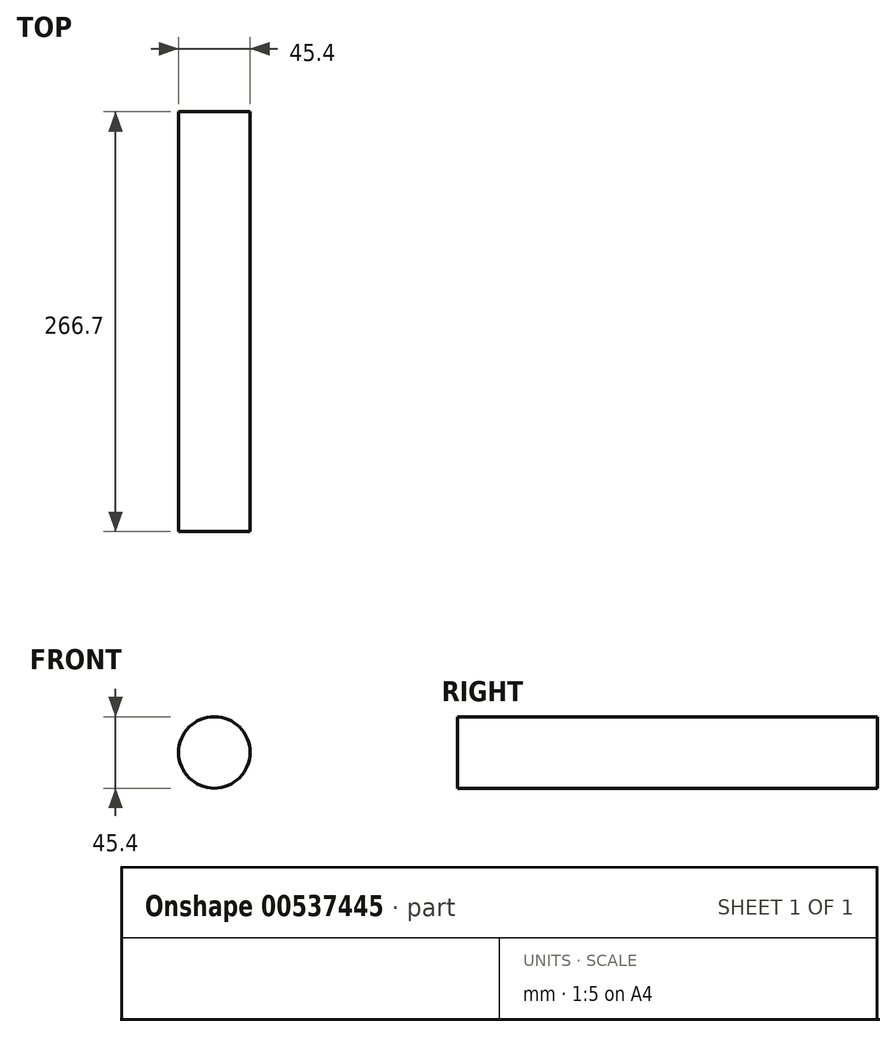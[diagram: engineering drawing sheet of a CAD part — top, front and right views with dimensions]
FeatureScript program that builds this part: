
annotation { "Feature Type Name" : "Feature", "Feature Type Description" : "" }
export const myFeature = defineFeature(function(context is Context, id is Id, definition is map)
    precondition{}
    {
        {
            var Q0;
            Q0=qCreatedBy(makeId("Front.planeOp"),FACE);
            var sketch = newSketch(context, id + "F0", { "sketchPlane" : qUnion([Q0])});
            skCircle(sketch, "E0", {"center": v(0, 0) * mm, "radius": 22.7 * mm});
            skSolve(sketch);
        }
        {
            var Q0;
            Q0 = qSketchRegion(id + "F0", true);
            extrude(context, id + "F1", {"entities" : qUnion([Q0]), "depth" : 266.7 * mm, "offsetDistance" : 25.4 * mm});
        }
    });
